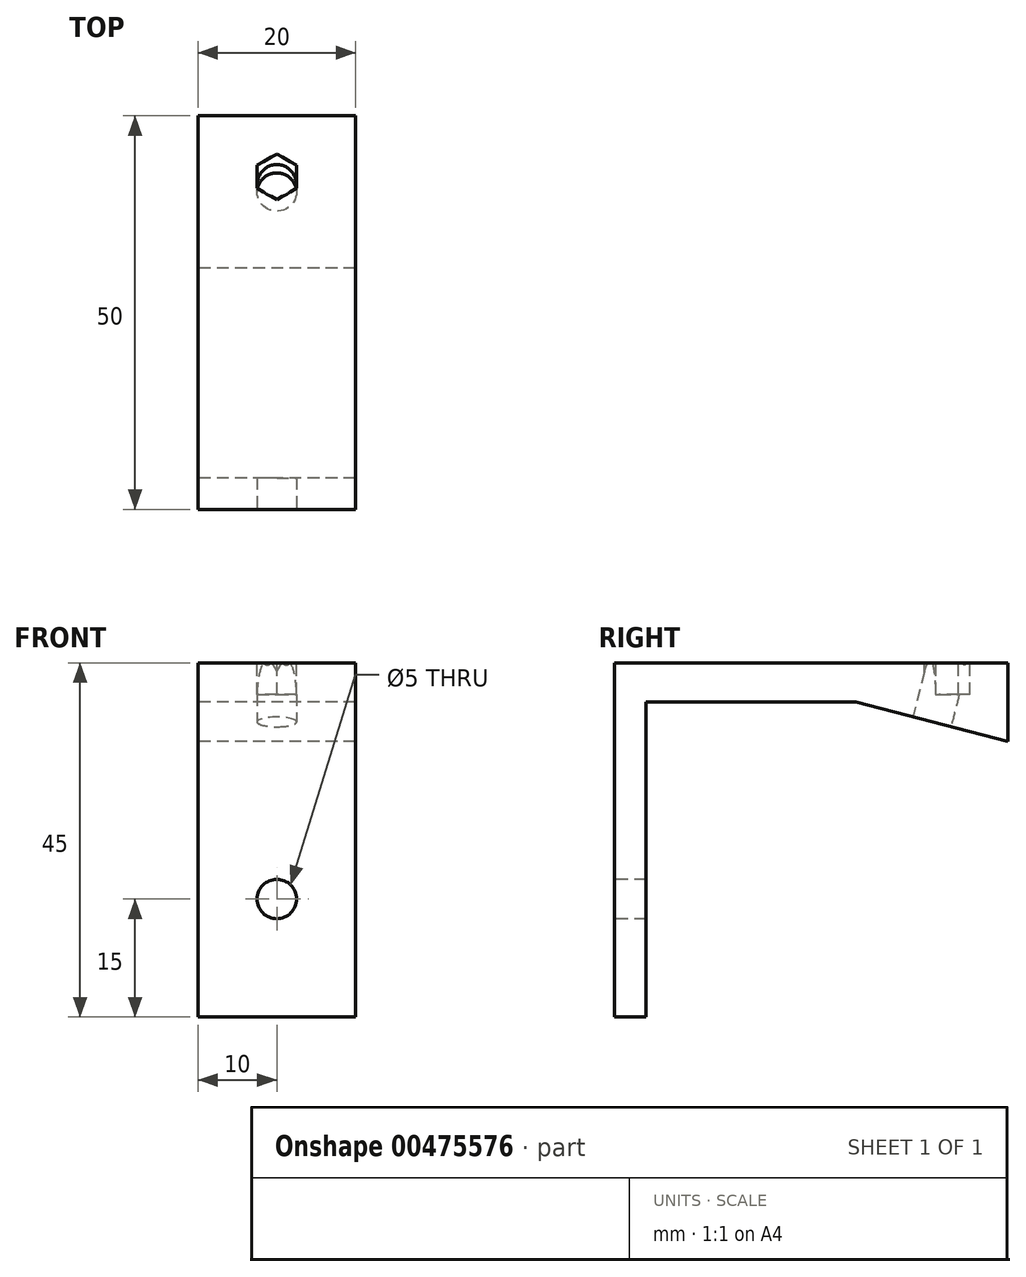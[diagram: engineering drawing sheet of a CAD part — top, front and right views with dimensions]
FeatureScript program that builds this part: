
annotation { "Feature Type Name" : "Feature", "Feature Type Description" : "" }
export const myFeature = defineFeature(function(context is Context, id is Id, definition is map)
    precondition{}
    {
        {
            var Q0;
            Q0=qCreatedBy(makeId("Right.planeOp"),FACE);
            var sketch = newSketch(context, id + "F0", { "sketchPlane" : qUnion([Q0])});
            skLineSegment(sketch, "E0.bottom", {"start": v(27.68, 0) * mm, "end": v(-22.32, 0) * mm});
            skLineSegment(sketch, "E0.top", {"start": v(27.68, 5) * mm, "end": v(-22.32, 5) * mm});
            skLineSegment(sketch, "E0.left", {"start": v(27.68, 0) * mm, "end": v(27.68, 5) * mm});
            skLineSegment(sketch, "E0.right", {"start": v(-22.32, 0) * mm, "end": v(-22.32, 5) * mm});
            skLineSegment(sketch, "E1.bottom", {"start": v(-22.32, 0) * mm, "end": v(-18.32, 0) * mm});
            skLineSegment(sketch, "E1.top", {"start": v(-22.32, -40) * mm, "end": v(-18.32, -40) * mm});
            skLineSegment(sketch, "E1.left", {"start": v(-22.32, 0) * mm, "end": v(-22.32, -40) * mm});
            skLineSegment(sketch, "E1.right", {"start": v(-18.32, 0) * mm, "end": v(-18.32, -40) * mm});
            skLineSegment(sketch, "E2", {"start": v(27.68, 0) * mm, "end": v(27.68, -5) * mm});
            skLineSegment(sketch, "E3", {"start": v(27.68, -5) * mm, "end": v(8.31, 0) * mm});
            skSolve(sketch);
        }
        {
            var Q0;
            Q0 = qSketchRegion(id + "F0", true);
            extrude(context, id + "F1", {"entities" : qUnion([Q0]), "depth" : 20 * mm, "offsetDistance" : 25 * mm});
        }
        {
            var Q0;
            Q0=makeQuery(id+"F1.opExtrude","SWEPT_FACE",FACE,{"disambiguationData":[OSD([sQuery(id+"F0.wireOp",EDGE,"E0.right"),sQuery(id+"F0.wireOp",EDGE,"E1.left")])]});
            var sketch = newSketch(context, id + "F2", { "sketchPlane" : qUnion([Q0])});
            skCircle(sketch, "E4", {"center": v(10, -25) * mm, "radius": 2.5 * mm});
            skSolve(sketch);
        }
        {
            var Q0;
            Q0 = qSketchRegion(id + "F2", true);
            extrude(context, id + "F3", {"entities" : qUnion([Q0]), "operationType" : NewBodyOperationType.REMOVE, "oppositeDirection" : true, "depth" : 5 * mm, "offsetDistance" : 25 * mm});
        }
        {
            var Q0;
            Q0=makeQuery(id+"F1.opExtrude","SWEPT_FACE",FACE,{"disambiguationData":[OSD([sQuery(id+"F0.wireOp",EDGE,"E3")])]});
            var sketch = newSketch(context, id + "F4", { "sketchPlane" : qUnion([Q0])});
            skCircle(sketch, "E5", {"center": v(10, -18.05) * mm, "radius": 2.5 * mm});
            skSolve(sketch);
        }
        {
            var Q0;
            Q0 = qSketchRegion(id + "F4", true);
            extrude(context, id + "F5", {"entities" : qUnion([Q0]), "operationType" : NewBodyOperationType.REMOVE, "oppositeDirection" : true, "depth" : 10 * mm, "offsetDistance" : 25 * mm});
        }
        {
            var Q0;
            Q0=makeQuery(id+"F1.opExtrude","SWEPT_FACE",FACE,{"disambiguationData":[OSD([sQuery(id+"F0.wireOp",EDGE,"E0.top")])]});
            var sketch = newSketch(context, id + "F6", { "sketchPlane" : qUnion([Q0])});
            skCircle(sketch, "E6.cCircle", {"center": v(10, 19.93) * mm, "radius": 2.5 * mm, "construction": true});
            skLineSegment(sketch, "E6.0", {"start": v(12.5, 21.38) * mm, "end": v(12.5, 18.5) * mm});
            skLineSegment(sketch, "E6.1", {"start": v(12.5, 18.5) * mm, "end": v(10, 17.05) * mm});
            skLineSegment(sketch, "E6.2", {"start": v(10, 17.05) * mm, "end": v(7.5, 18.5) * mm});
            skLineSegment(sketch, "E6.3", {"start": v(7.5, 18.5) * mm, "end": v(7.5, 21.38) * mm});
            skLineSegment(sketch, "E6.4", {"start": v(7.5, 21.38) * mm, "end": v(10, 22.82) * mm});
            skLineSegment(sketch, "E6.5", {"start": v(10, 22.82) * mm, "end": v(12.5, 21.38) * mm});
            skPoint(sketch, "E6.0.midPoint", {"position": v(12.5, 19.93) * mm});
            skSolve(sketch);
        }
        {
            var Q0;
            Q0 = qSketchRegion(id + "F6", true);
            extrude(context, id + "F7", {"entities" : qUnion([Q0]), "operationType" : NewBodyOperationType.REMOVE, "oppositeDirection" : true, "depth" : 4 * mm, "offsetDistance" : 25 * mm});
        }
    });
